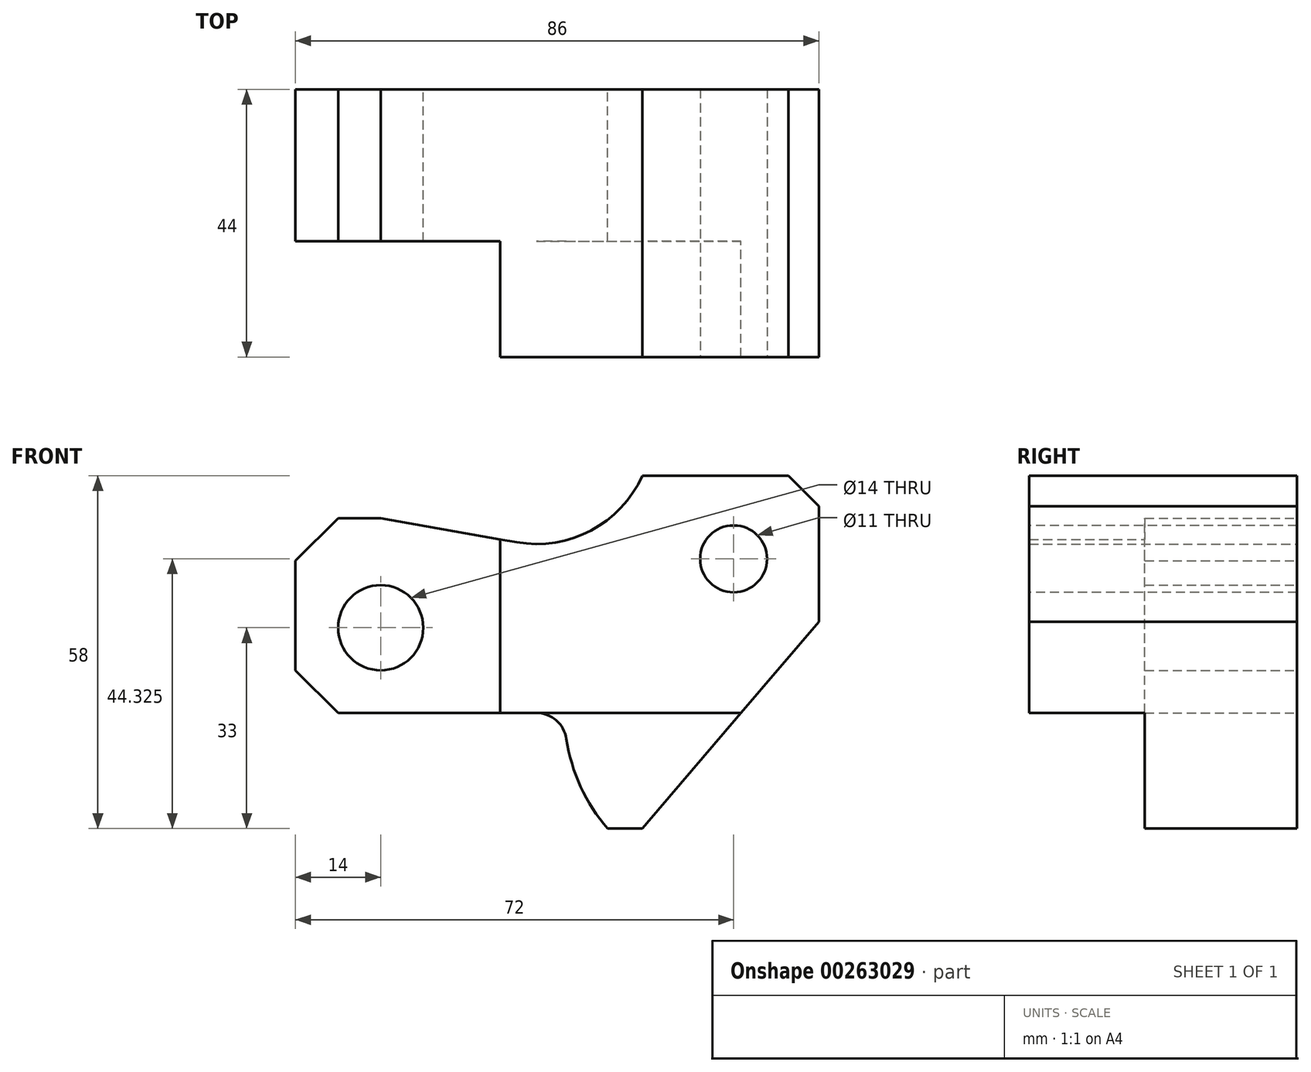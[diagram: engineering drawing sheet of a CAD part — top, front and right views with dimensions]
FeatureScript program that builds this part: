
annotation { "Feature Type Name" : "Feature", "Feature Type Description" : "" }
export const myFeature = defineFeature(function(context is Context, id is Id, definition is map)
    precondition{}
    {
        {
            var Q0;
            Q0=qCreatedBy(makeId("Front.planeOp"),FACE);
            var sketch = newSketch(context, id + "F0", { "sketchPlane" : qUnion([Q0])});
            skCircle(sketch, "E0", {"center": v(0, 0) * mm, "radius": 7 * mm});
            skLineSegment(sketch, "E1", {"start": v(-14, 11) * mm, "end": v(-7, 18) * mm});
            skLineSegment(sketch, "E2", {"start": v(-7, 18) * mm, "end": v(0, 18) * mm});
            skLineSegment(sketch, "E3", {"start": v(0, 18) * mm, "end": v(22.36, 14.06) * mm});
            skArc(sketch, "E4", {"start": v(22.36, 14.06) * mm, "mid": v(34.56, 15.98) * mm, "end": v(43, 25) * mm});
            skLineSegment(sketch, "E5", {"start": v(43, 25) * mm, "end": v(67, 25) * mm});
            skLineSegment(sketch, "E6", {"start": v(67, 25) * mm, "end": v(72, 20) * mm});
            skLineSegment(sketch, "E7", {"start": v(72, 20) * mm, "end": v(72, 1) * mm});
            skLineSegment(sketch, "E8", {"start": v(72, 1) * mm, "end": v(43, -33) * mm});
            skLineSegment(sketch, "E9", {"start": v(43, -33) * mm, "end": v(43, -33) * mm});
            skLineSegment(sketch, "E10", {"start": v(25.58, -14) * mm, "end": v(-7, -14) * mm});
            skLineSegment(sketch, "E11", {"start": v(-7, -14) * mm, "end": v(-14, -7) * mm});
            skLineSegment(sketch, "E12", {"start": v(-14, -7) * mm, "end": v(-14, 11) * mm});
            skLineSegment(sketch, "E13", {"start": v(0, 18) * mm, "end": v(22.3, 18) * mm, "construction": true});
            skLineSegment(sketch, "E14", {"start": v(43, -33) * mm, "end": v(37.3, -33) * mm});
            skArc(sketch, "E15", {"start": v(30.52, -18.26) * mm, "mid": v(32.86, -26.12) * mm, "end": v(37.3, -33) * mm});
            skArc(sketch, "E16", {"start": v(30.52, -18.26) * mm, "mid": v(28.84, -15.21) * mm, "end": v(25.58, -14) * mm});
            skLineSegment(sketch, "E17", {"start": v(20, 14.47) * mm, "end": v(20, -14) * mm});
            skLineSegment(sketch, "E18", {"start": v(-14, -7) * mm, "end": v(-14, -32.47) * mm, "construction": true});
            skLineSegment(sketch, "E19", {"start": v(-14, 11) * mm, "end": v(-14, 34.2) * mm, "construction": true});
            skSolve(sketch);
        }
        {
            var Q0;
            Q0=qSketchRegion(id+"F0",true);
            extrude(context, id + "F1", {"entities" : qUnion([Q0]), "depth" : 44 * mm});
        }
        {
            var Q0;
            Q0=makeQuery(id+"F1.opExtrude","SWEPT_FACE",FACE,{"disambiguationData":[OSD([sQuery(id+"F0.wireOp",EDGE,"E2")])]});
            var sketch = newSketch(context, id + "F2", { "sketchPlane" : qUnion([Q0])});
            skLineSegment(sketch, "E20.bottom", {"start": v(-14.34, -44) * mm, "end": v(19.66, -44) * mm});
            skLineSegment(sketch, "E20.top", {"start": v(-14.34, -25) * mm, "end": v(19.66, -25) * mm});
            skLineSegment(sketch, "E20.left", {"start": v(-14.34, -44) * mm, "end": v(-14.34, -25) * mm});
            skLineSegment(sketch, "E20.right", {"start": v(19.66, -44) * mm, "end": v(19.66, -25) * mm});
            skSolve(sketch);
        }
        {
            var Q0;
            Q0 = qSketchRegion(id + "F2", true);
            extrude(context, id + "F3", {"entities" : qUnion([Q0]), "operationType" : NewBodyOperationType.REMOVE, "endBound" : BoundingType.THROUGH_ALL, "oppositeDirection" : true, "depth" : 25 * mm});
        }
        {
            var Q0;
            Q0=makeQuery(id+"F1.opExtrude","CAP_FACE",FACE,{"disambiguationData":[OSD([sQuery(id+"F0.wireOp",EDGE,"E0"),sQuery(id+"F0.wireOp",EDGE,"E1"),sQuery(id+"F0.wireOp",EDGE,"E2"),sQuery(id+"F0.wireOp",EDGE,"E3"),sQuery(id+"F0.wireOp",EDGE,"E4"),sQuery(id+"F0.wireOp",EDGE,"E5"),sQuery(id+"F0.wireOp",EDGE,"E6"),sQuery(id+"F0.wireOp",EDGE,"E7"),sQuery(id+"F0.wireOp",EDGE,"E8"),sQuery(id+"F0.wireOp",EDGE,"E10"),sQuery(id+"F0.wireOp",EDGE,"E11"),sQuery(id+"F0.wireOp",EDGE,"E12"),sQuery(id+"F0.wireOp",EDGE,"E14"),sQuery(id+"F0.wireOp",EDGE,"E15"),sQuery(id+"F0.wireOp",EDGE,"E16")])],"isStart":false});
            var sketch = newSketch(context, id + "F4", { "sketchPlane" : qUnion([Q0])});
            skLineSegment(sketch, "E21.bottom", {"start": v(25.58, -14) * mm, "end": v(61.12, -14) * mm});
            skLineSegment(sketch, "E21.top", {"start": v(25.58, -33) * mm, "end": v(61.12, -33) * mm});
            skLineSegment(sketch, "E21.left", {"start": v(25.58, -14) * mm, "end": v(25.58, -33) * mm});
            skLineSegment(sketch, "E21.right", {"start": v(61.12, -14) * mm, "end": v(61.12, -33) * mm});
            skSolve(sketch);
        }
        {
            var Q0;
            Q0 = qSketchRegion(id + "F4", true);
            extrude(context, id + "F5", {"entities" : qUnion([Q0]), "operationType" : NewBodyOperationType.REMOVE, "oppositeDirection" : true, "depth" : 19 * mm});
        }
        {
            var Q0;
            Q0=makeQuery(id+"F1.opExtrude","CAP_FACE",FACE,{"disambiguationData":[OSD([sQuery(id+"F0.wireOp",EDGE,"E0"),sQuery(id+"F0.wireOp",EDGE,"E1"),sQuery(id+"F0.wireOp",EDGE,"E2"),sQuery(id+"F0.wireOp",EDGE,"E3"),sQuery(id+"F0.wireOp",EDGE,"E4"),sQuery(id+"F0.wireOp",EDGE,"E5"),sQuery(id+"F0.wireOp",EDGE,"E6"),sQuery(id+"F0.wireOp",EDGE,"E7"),sQuery(id+"F0.wireOp",EDGE,"E8"),sQuery(id+"F0.wireOp",EDGE,"E10"),sQuery(id+"F0.wireOp",EDGE,"E11"),sQuery(id+"F0.wireOp",EDGE,"E12"),sQuery(id+"F0.wireOp",EDGE,"E14"),sQuery(id+"F0.wireOp",EDGE,"E15"),sQuery(id+"F0.wireOp",EDGE,"E16")])],"isStart":false});
            var sketch = newSketch(context, id + "F6", { "sketchPlane" : qUnion([Q0])});
            skCircle(sketch, "E22", {"center": v(58, 11.33) * mm, "radius": 5.5 * mm});
            skSolve(sketch);
        }
        {
            var Q0;
            Q0 = qSketchRegion(id + "F6", true);
            extrude(context, id + "F7", {"entities" : qUnion([Q0]), "operationType" : NewBodyOperationType.REMOVE, "endBound" : BoundingType.THROUGH_ALL, "oppositeDirection" : true, "depth" : 25 * mm});
        }
    });
